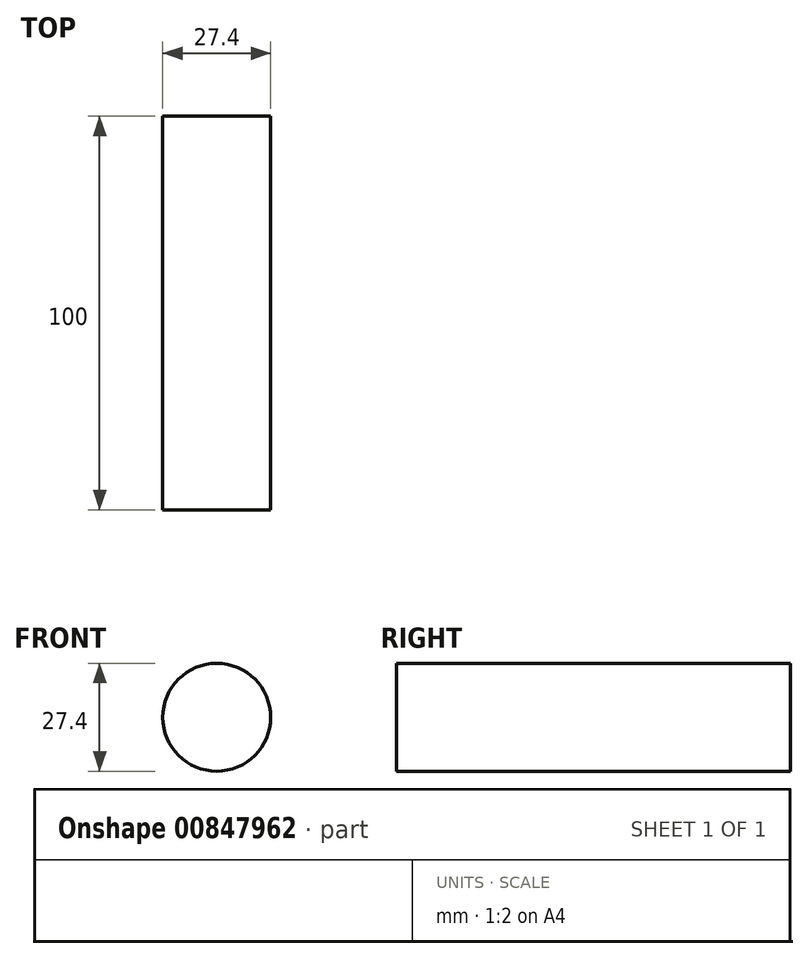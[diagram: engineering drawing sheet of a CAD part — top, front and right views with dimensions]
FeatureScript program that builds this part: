
annotation { "Feature Type Name" : "Feature", "Feature Type Description" : "" }
export const myFeature = defineFeature(function(context is Context, id is Id, definition is map)
    precondition{}
    {
        {
            var Q0;
            Q0=qCreatedBy(makeId("Front.planeOp"),FACE);
            var sketch = newSketch(context, id + "F0", { "sketchPlane" : qUnion([Q0])});
            skCircle(sketch, "E0", {"center": v(-50.38, 49.74) * mm, "radius": 13.7 * mm});
            skCircle(sketch, "E1", {"center": v(-50.38, 49.74) * mm, "radius": 12.47 * mm});
            skSolve(sketch);
        }
        {
            var Q0;
            Q0=sQuery(id+"F0.wireOp",EDGE,"E0");
            extrude(context, id + "F1", {"bodyType" : ToolBodyType.SURFACE, "surfaceEntities" : qUnion([Q0]), "depth" : 100 * mm, "offsetDistance" : 25.4 * mm});
        }
    });
